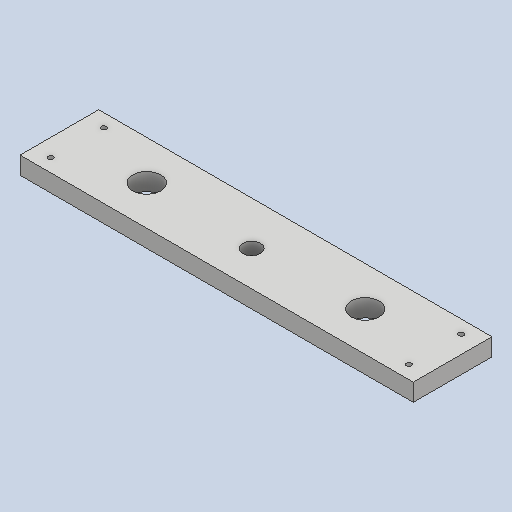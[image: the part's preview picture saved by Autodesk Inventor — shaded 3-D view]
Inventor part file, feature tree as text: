
AUTODESK INVENTOR PART (.ipt)
format: ipt  version: 2023 (Build 270158000, 158)  size: 117,248 bytes
history: native  units: mm
features: extrude x1, sketch x1
ambient origin geometry x8: Origin, YZ Plane, XZ Plane, XY Plane, X Axis, Y Axis, Z Axis, Center Point
bodies: Solid1 (feature_tree)
feature tree (2):
  extrude  "Extrusion1"  Depth=225.0mm
  sketch  "Sketch1"  dims[d0=45.0mm d1=225.0mm d2=30.0mm d3=3.0mm d4=3.0mm d5=7.5mm d6=7.5mm d7=3.0mm d8=3.0mm d9=30.0mm d10=10.0mm d11=10.0mm d12=10.0mm d13=0.0mm d14=16.0mm d15=16.0mm d16=22.5mm d17=22.5mm d18=50.0mm d19=50.0mm d20=10.2mm d21=25.0mm d22=112.5mm]
